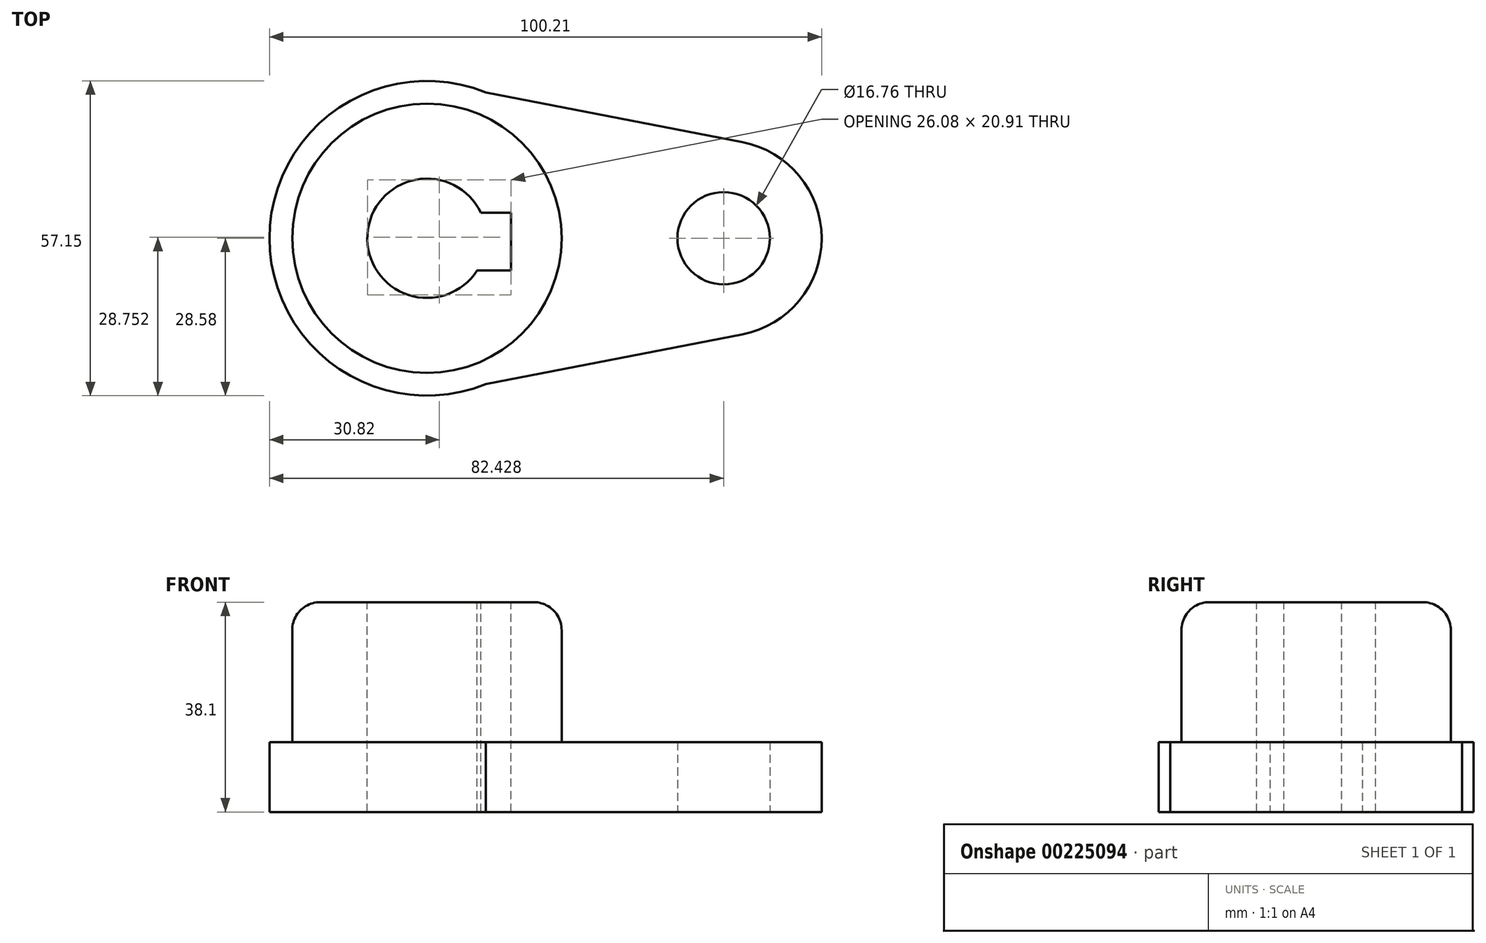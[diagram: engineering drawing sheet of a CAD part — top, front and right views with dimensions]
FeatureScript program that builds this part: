
annotation { "Feature Type Name" : "Feature", "Feature Type Description" : "" }
export const myFeature = defineFeature(function(context is Context, id is Id, definition is map)
    precondition{}
    {
        {
            var Q0;
            Q0=qCreatedBy(makeId("Top.planeOp"),FACE);
            var sketch = newSketch(context, id + "F0", { "sketchPlane" : qUnion([Q0])});
            skCircle(sketch, "E0", {"center": v(0, 0) * mm, "radius": 28.58 * mm});
            skCircle(sketch, "E1", {"center": v(53.85, 0) * mm, "radius": 17.78 * mm});
            skCircle(sketch, "E2", {"center": v(53.85, 0) * mm, "radius": 8.38 * mm});
            skLineSegment(sketch, "E3", {"start": v(0, 28.58) * mm, "end": v(57.24, 17.45) * mm});
            skLineSegment(sketch, "E4", {"start": v(0, -28.58) * mm, "end": v(57.24, -17.45) * mm});
            skSolve(sketch);
        }
        {
            var Q0;
            Q0 = qSketchRegion(id + "F0", true);
            extrude(context, id + "F1", {"entities" : qUnion([Q0]), "depth" : 12.7 * mm});
        }
        {
            var Q0;
            Q0=makeQuery(id+"F1.opExtrude","CAP_FACE",FACE,{"disambiguationData":[OSD([sQuery(id+"F0.wireOp",EDGE,"E0"),sQuery(id+"F0.wireOp",EDGE,"E1"),sQuery(id+"F0.wireOp",EDGE,"E2"),sQuery(id+"F0.wireOp",EDGE,"E3"),sQuery(id+"F0.wireOp",EDGE,"E4")])],"isStart":false});
            var sketch = newSketch(context, id + "F2", { "sketchPlane" : qUnion([Q0])});
            skCircle(sketch, "E5", {"center": v(0, 0) * mm, "radius": 24.44 * mm});
            skSolve(sketch);
        }
        {
            var Q0;
            Q0 = qSketchRegion(id + "F2", true);
            extrude(context, id + "F3", {"entities" : qUnion([Q0]), "operationType" : NewBodyOperationType.ADD, "depth" : 25.4 * mm});
        }
        {
            var Q0;
            Q0=makeQuery(id+"F3.opExtrude","CAP_FACE",FACE,{"disambiguationData":[OSD([sQuery(id+"F2.wireOp",EDGE,"E5")])],"isStart":false});
            fillet(context, id + "F4", {"entities" : qUnion([Q0]), "radius" : 5.08 * mm, "tangentPropagation" : true, "allowEdgeOverflow" : false});
        }
        {
            var Q0;
            Q0=makeQuery(id+"F3.opExtrude","CAP_FACE",FACE,{"disambiguationData":[OSD([sQuery(id+"F2.wireOp",EDGE,"E5")])],"isStart":false});
            var sketch = newSketch(context, id + "F5", { "sketchPlane" : qUnion([Q0])});
            skCircle(sketch, "E6", {"center": v(0, 0) * mm, "radius": 10.82 * mm});
            skLineSegment(sketch, "E7", {"start": v(9.1, -5.84) * mm, "end": v(15.28, -5.84) * mm});
            skLineSegment(sketch, "E8", {"start": v(15.28, -5.84) * mm, "end": v(15.28, 4.65) * mm});
            skLineSegment(sketch, "E9", {"start": v(15.28, 4.65) * mm, "end": v(9.77, 4.65) * mm});
            skArc(sketch, "E10", {"start": v(9.1, -5.84) * mm, "mid": v(10.34, -0.66) * mm, "end": v(9.77, 4.65) * mm});
            skSolve(sketch);
        }
        {
            var Q0;
            Q0 = qSketchRegion(id + "F5", true);
            extrude(context, id + "F6", {"entities" : qUnion([Q0]), "operationType" : NewBodyOperationType.REMOVE, "endBound" : BoundingType.THROUGH_ALL, "oppositeDirection" : true, "depth" : 25.4 * mm});
        }
    });
